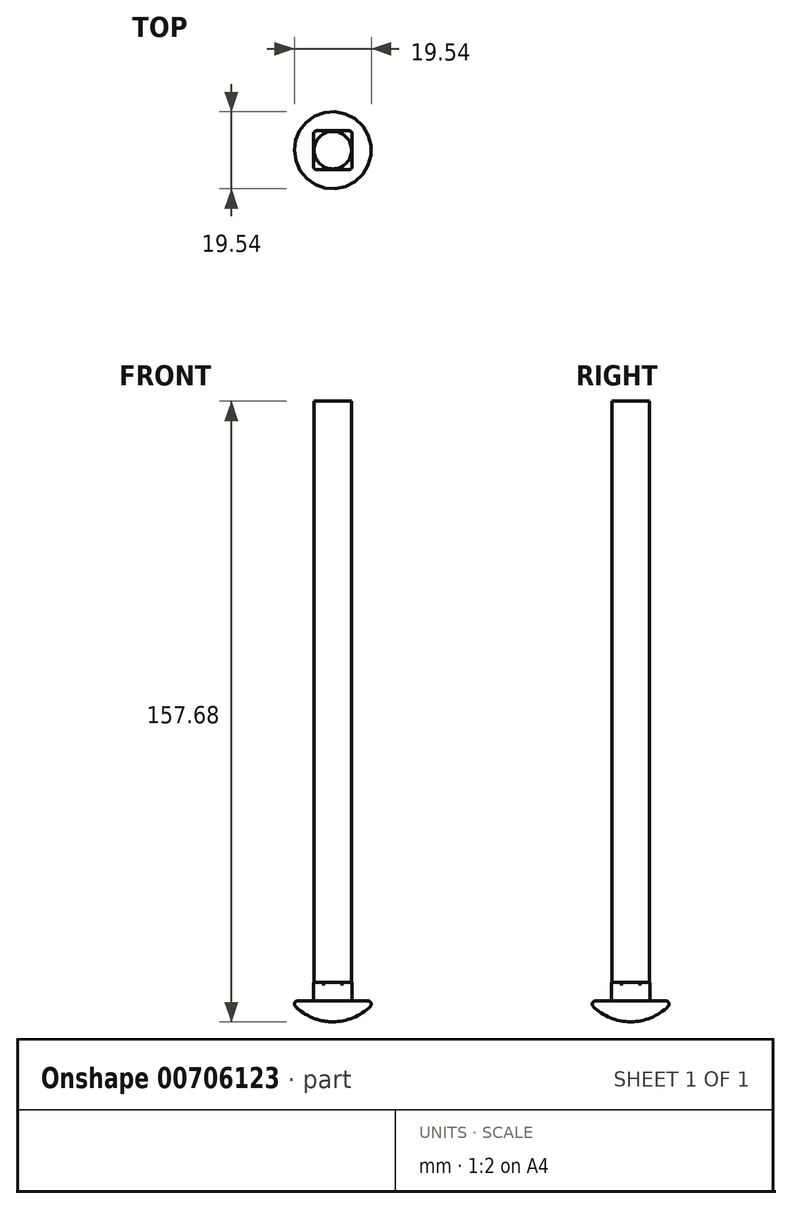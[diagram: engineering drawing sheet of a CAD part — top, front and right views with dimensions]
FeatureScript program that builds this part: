
annotation { "Feature Type Name" : "Feature", "Feature Type Description" : "" }
export const myFeature = defineFeature(function(context is Context, id is Id, definition is map)
    precondition{}
    {
        {
            var Q0;
            Q0=qCreatedBy(makeId("Front.planeOp"),FACE);
            var sketch = newSketch(context, id + "F0", { "sketchPlane" : qUnion([Q0])});
            skLineSegment(sketch, "E0", {"start": v(0, 0) * mm, "end": v(0, 5.28) * mm});
            skLineSegment(sketch, "E1", {"start": v(0, 5.28) * mm, "end": v(10.72, 5.28) * mm});
            skArc(sketch, "E2", {"start": v(0, 0) * mm, "mid": v(5.98, 1.4) * mm, "end": v(10.72, 5.28) * mm});
            skLineSegment(sketch, "E3", {"start": v(0, 5.28) * mm, "end": v(0, 157.68) * mm});
            skLineSegment(sketch, "E4", {"start": v(0, 157.68) * mm, "end": v(4.76, 157.68) * mm});
            skLineSegment(sketch, "E5", {"start": v(4.76, 157.68) * mm, "end": v(4.76, 5.28) * mm});
            skSolve(sketch);
        }
        {
            var Q0;
            {var subQ0=sQuery(id+"F0.wireOp",EDGE,"E3");Q0=makeQuery(id+"F0.imprint","IMPRINT",FACE,{"disambiguationData":[TD([[makeQuery(id+"F0.imprint","IMPRINT",EDGE,{"derivedFrom":subQ0}),-1.0]])]});}
            var Q1;
            {var subQ0=sQuery(id+"F0.wireOp",EDGE,"E0");Q1=makeQuery(id+"F0.imprint","IMPRINT",FACE,{"disambiguationData":[TD([[makeQuery(id+"F0.imprint","IMPRINT",EDGE,{"derivedFrom":subQ0}),-1.0]])]});}
            var Q2;
            Q2=sQuery(id+"F0.wireOp",EDGE,"E3");
            revolve(context, id + "F1", {"surfaceOperationType" : NewSurfaceOperationType.NEW, "entities" : qUnion([Q0, Q1]), "axis" : qUnion([Q2]), "revolveType" : RevolveType.FULL});
        }
        {
            var Q0;
            Q0=makeQuery(id+"F1.opRevolve","SWEPT_EDGE",EDGE,{"disambiguationData":[OSD([sQuery(id+"F0.wireOp",EDGE,"E1"),sQuery(id+"F0.wireOp",EDGE,"E2")])]});
            fillet(context, id + "F2", {"entities" : qUnion([Q0]), "radius" : 0.79 * mm, "tangentPropagation" : true, "allowEdgeOverflow" : false});
        }
        {
            var Q0;
            Q0=makeQuery(id+"F1.opRevolve","SWEPT_FACE",FACE,{"disambiguationData":[OSD([sQuery(id+"F0.wireOp",EDGE,"E1")])]});
            var sketch = newSketch(context, id + "F3", { "sketchPlane" : qUnion([Q0])});
            skLineSegment(sketch, "E6.bottom", {"start": v(4.93, -4.93) * mm, "end": v(-4.93, -4.93) * mm});
            skLineSegment(sketch, "E6.top", {"start": v(4.93, 4.93) * mm, "end": v(-4.93, 4.93) * mm});
            skLineSegment(sketch, "E6.left", {"start": v(4.93, -4.93) * mm, "end": v(4.93, 4.93) * mm});
            skLineSegment(sketch, "E6.right", {"start": v(-4.93, -4.93) * mm, "end": v(-4.93, 4.93) * mm});
            skPoint(sketch, "E6.middle", {"position": v(0, 0) * mm});
            skSolve(sketch);
        }
        {
            var Q0;
            Q0=makeQuery(id+"F3.imprint","IMPRINT",FACE,{"disambiguationData":[TD([[makeQuery(id+"F3.imprint","IMPRINT",EDGE,{"derivedFrom":sQuery(id+"F3.wireOp",EDGE,"E6.bottom")}),-1.0]])]});
            extrude(context, id + "F4", {"entities" : qUnion([Q0]), "operationType" : NewBodyOperationType.ADD, "depth" : 4.78 * mm, "offsetDistance" : 25.4 * mm});
        }
        {
            var Q0;
            Q0=makeQuery(id+"F4.opExtrude","CAP_EDGE",EDGE,{"disambiguationData":[OSD([sQuery(id+"F0.wireOp",EDGE,"E1"),sQuery(id+"F0.wireOp",EDGE,"E5")])],"isStart":false});
            var Q1;
            Q1=makeQuery(id+"F4.opExtrude","CAP_EDGE",EDGE,{"disambiguationData":[OSD([sQuery(id+"F3.wireOp",EDGE,"E6.left")])],"isStart":true});
            var Q2;
            Q2=makeQuery(id+"F4.opExtrude","CAP_EDGE",EDGE,{"disambiguationData":[OSD([sQuery(id+"F3.wireOp",EDGE,"E6.bottom")])],"isStart":true});
            var Q3;
            Q3=makeQuery(id+"F4.opExtrude","CAP_EDGE",EDGE,{"disambiguationData":[OSD([sQuery(id+"F3.wireOp",EDGE,"E6.top")])],"isStart":true});
            var Q4;
            Q4=makeQuery(id+"F4.opExtrude","CAP_EDGE",EDGE,{"disambiguationData":[OSD([sQuery(id+"F3.wireOp",EDGE,"E6.right")])],"isStart":true});
            var Q5;
            Q5=makeQuery(id+"F4.opExtrude","SWEPT_EDGE",EDGE,{"disambiguationData":[OSD([sQuery(id+"F3.wireOp",EDGE,"E6.top"),sQuery(id+"F3.wireOp",EDGE,"E6.right")])]});
            var Q6;
            Q6=makeQuery(id+"F4.opExtrude","SWEPT_EDGE",EDGE,{"disambiguationData":[OSD([sQuery(id+"F3.wireOp",EDGE,"E6.bottom"),sQuery(id+"F3.wireOp",EDGE,"E6.right")])]});
            var Q7;
            Q7=makeQuery(id+"F4.opExtrude","SWEPT_EDGE",EDGE,{"disambiguationData":[OSD([sQuery(id+"F3.wireOp",EDGE,"E6.bottom"),sQuery(id+"F3.wireOp",EDGE,"E6.left")])]});
            var Q8;
            Q8=makeQuery(id+"F4.opExtrude","SWEPT_EDGE",EDGE,{"disambiguationData":[OSD([sQuery(id+"F3.wireOp",EDGE,"E6.top"),sQuery(id+"F3.wireOp",EDGE,"E6.left")])]});
            fillet(context, id + "F5", {"entities" : qUnion([Q0, Q1, Q2, Q3, Q4, Q5, Q6, Q7, Q8]), "radius" : 0.79 * mm, "tangentPropagation" : true, "allowEdgeOverflow" : false});
        }
        {
            var Q0;
            Q0=makeQuery(id+"F4.opExtrude","CAP_EDGE",EDGE,{"disambiguationData":[OSD([sQuery(id+"F3.wireOp",EDGE,"E6.right")])],"isStart":false});
            var Q1;
            {var subQ0=sQuery(id+"F3.wireOp",EDGE,"E6.left");var subQ1=sQuery(id+"F3.wireOp",EDGE,"E6.bottom");Q1=makeQuery(id+"F5.opFillet","BLEND_EDGE",EDGE,{"blendedFrom":[makeQuery(id+"F4.opExtrude","SWEPT_EDGE",EDGE,{"disambiguationData":[OSD([subQ1,subQ0])]}),makeQuery(id+"F4.opExtrude","CAP_FACE",FACE,{"disambiguationData":[OSD([sQuery(id+"F0.wireOp",EDGE,"E1"),sQuery(id+"F0.wireOp",EDGE,"E5"),subQ1,sQuery(id+"F3.wireOp",EDGE,"E6.top"),subQ0,sQuery(id+"F3.wireOp",EDGE,"E6.right")])],"isStart":false})],"blendedInto":[makeQuery(id+"F4.opExtrude","CAP_FACE",FACE,{"disambiguationData":[OSD([sQuery(id+"F0.wireOp",EDGE,"E1"),sQuery(id+"F0.wireOp",EDGE,"E5"),subQ1,sQuery(id+"F3.wireOp",EDGE,"E6.top"),subQ0,sQuery(id+"F3.wireOp",EDGE,"E6.right")])],"isStart":false})]});}
            var Q2;
            Q2=makeQuery(id+"F4.opExtrude","CAP_EDGE",EDGE,{"disambiguationData":[OSD([sQuery(id+"F3.wireOp",EDGE,"E6.bottom")])],"isStart":false});
            var Q3;
            Q3=makeQuery(id+"F4.opExtrude","CAP_EDGE",EDGE,{"disambiguationData":[OSD([sQuery(id+"F3.wireOp",EDGE,"E6.bottom")])],"isStart":false});
            var Q4;
            Q4=makeQuery(id+"F5.opFillet","BLEND_EDGE",EDGE,{"blendedFrom":[makeQuery(id+"F4.opExtrude","CAP_EDGE",EDGE,{"disambiguationData":[OSD([sQuery(id+"F0.wireOp",EDGE,"E1"),sQuery(id+"F0.wireOp",EDGE,"E5")])],"isStart":false}),makeQuery(id+"F4.opExtrude","SWEPT_FACE",FACE,{"disambiguationData":[OSD([sQuery(id+"F3.wireOp",EDGE,"E6.bottom")])]})],"blendedInto":[makeQuery(id+"F4.opExtrude","SWEPT_FACE",FACE,{"disambiguationData":[OSD([sQuery(id+"F3.wireOp",EDGE,"E6.bottom")])]})]});
            var Q5;
            {var subQ0=sQuery(id+"F3.wireOp",EDGE,"E6.right");var subQ1=sQuery(id+"F3.wireOp",EDGE,"E6.bottom");Q5=makeQuery(id+"F5.opFillet","BLEND_EDGE",EDGE,{"blendedFrom":[makeQuery(id+"F4.opExtrude","SWEPT_EDGE",EDGE,{"disambiguationData":[OSD([subQ1,subQ0])]}),makeQuery(id+"F4.opExtrude","CAP_FACE",FACE,{"disambiguationData":[OSD([sQuery(id+"F0.wireOp",EDGE,"E1"),sQuery(id+"F0.wireOp",EDGE,"E5"),subQ1,sQuery(id+"F3.wireOp",EDGE,"E6.top"),sQuery(id+"F3.wireOp",EDGE,"E6.left"),subQ0])],"isStart":false})],"blendedInto":[makeQuery(id+"F4.opExtrude","CAP_FACE",FACE,{"disambiguationData":[OSD([sQuery(id+"F0.wireOp",EDGE,"E1"),sQuery(id+"F0.wireOp",EDGE,"E5"),subQ1,sQuery(id+"F3.wireOp",EDGE,"E6.top"),sQuery(id+"F3.wireOp",EDGE,"E6.left"),subQ0])],"isStart":false})]});}
            var Q6;
            Q6=makeQuery(id+"F5.opFillet","BLEND_EDGE",EDGE,{"blendedFrom":[makeQuery(id+"F4.opExtrude","CAP_EDGE",EDGE,{"disambiguationData":[OSD([sQuery(id+"F0.wireOp",EDGE,"E1"),sQuery(id+"F0.wireOp",EDGE,"E5")])],"isStart":false}),makeQuery(id+"F4.opExtrude","SWEPT_FACE",FACE,{"disambiguationData":[OSD([sQuery(id+"F3.wireOp",EDGE,"E6.right")])]})],"blendedInto":[makeQuery(id+"F4.opExtrude","SWEPT_FACE",FACE,{"disambiguationData":[OSD([sQuery(id+"F3.wireOp",EDGE,"E6.right")])]})]});
            var Q7;
            {var subQ0=sQuery(id+"F3.wireOp",EDGE,"E6.right");var subQ1=sQuery(id+"F3.wireOp",EDGE,"E6.top");Q7=makeQuery(id+"F5.opFillet","BLEND_EDGE",EDGE,{"blendedFrom":[makeQuery(id+"F4.opExtrude","SWEPT_EDGE",EDGE,{"disambiguationData":[OSD([subQ1,subQ0])]}),makeQuery(id+"F4.opExtrude","CAP_FACE",FACE,{"disambiguationData":[OSD([sQuery(id+"F0.wireOp",EDGE,"E1"),sQuery(id+"F0.wireOp",EDGE,"E5"),sQuery(id+"F3.wireOp",EDGE,"E6.bottom"),subQ1,sQuery(id+"F3.wireOp",EDGE,"E6.left"),subQ0])],"isStart":false})],"blendedInto":[makeQuery(id+"F4.opExtrude","CAP_FACE",FACE,{"disambiguationData":[OSD([sQuery(id+"F0.wireOp",EDGE,"E1"),sQuery(id+"F0.wireOp",EDGE,"E5"),sQuery(id+"F3.wireOp",EDGE,"E6.bottom"),subQ1,sQuery(id+"F3.wireOp",EDGE,"E6.left"),subQ0])],"isStart":false})]});}
            var Q8;
            Q8=makeQuery(id+"F4.opExtrude","CAP_EDGE",EDGE,{"disambiguationData":[OSD([sQuery(id+"F3.wireOp",EDGE,"E6.top")])],"isStart":false});
            var Q9;
            Q9=makeQuery(id+"F5.opFillet","BLEND_EDGE",EDGE,{"blendedFrom":[makeQuery(id+"F4.opExtrude","CAP_EDGE",EDGE,{"disambiguationData":[OSD([sQuery(id+"F0.wireOp",EDGE,"E1"),sQuery(id+"F0.wireOp",EDGE,"E5")])],"isStart":false}),makeQuery(id+"F4.opExtrude","SWEPT_FACE",FACE,{"disambiguationData":[OSD([sQuery(id+"F3.wireOp",EDGE,"E6.top")])]})],"blendedInto":[makeQuery(id+"F4.opExtrude","SWEPT_FACE",FACE,{"disambiguationData":[OSD([sQuery(id+"F3.wireOp",EDGE,"E6.top")])]})]});
            var Q10;
            Q10=makeQuery(id+"F4.opExtrude","CAP_EDGE",EDGE,{"disambiguationData":[OSD([sQuery(id+"F3.wireOp",EDGE,"E6.left")])],"isStart":false});
            var Q11;
            Q11=makeQuery(id+"F5.opFillet","BLEND_EDGE",EDGE,{"blendedFrom":[makeQuery(id+"F4.opExtrude","CAP_EDGE",EDGE,{"disambiguationData":[OSD([sQuery(id+"F0.wireOp",EDGE,"E1"),sQuery(id+"F0.wireOp",EDGE,"E5")])],"isStart":false}),makeQuery(id+"F4.opExtrude","SWEPT_FACE",FACE,{"disambiguationData":[OSD([sQuery(id+"F3.wireOp",EDGE,"E6.left")])]})],"blendedInto":[makeQuery(id+"F4.opExtrude","SWEPT_FACE",FACE,{"disambiguationData":[OSD([sQuery(id+"F3.wireOp",EDGE,"E6.left")])]})]});
            fillet(context, id + "F6", {"entities" : qUnion([Q0, Q1, Q2, Q3, Q4, Q5, Q6, Q7, Q8, Q9, Q10, Q11]), "radius" : 0.79 * mm, "tangentPropagation" : true, "allowEdgeOverflow" : false});
        }
    });
